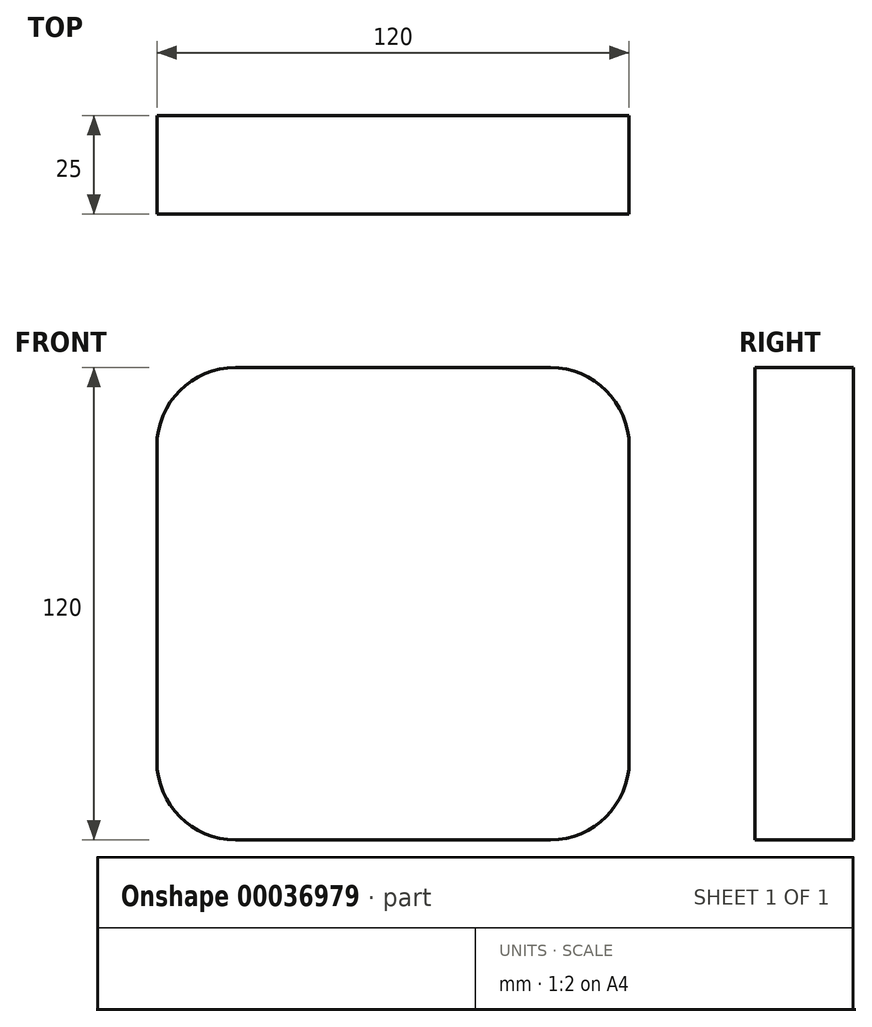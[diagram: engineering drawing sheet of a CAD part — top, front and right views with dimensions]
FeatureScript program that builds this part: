
annotation { "Feature Type Name" : "Feature", "Feature Type Description" : "" }
export const myFeature = defineFeature(function(context is Context, id is Id, definition is map)
    precondition{}
    {
        {
            var Q0;
            Q0=qCreatedBy(makeId("Front.planeOp"),FACE);
            var sketch = newSketch(context, id + "F0", { "sketchPlane" : qUnion([Q0])});
            skLineSegment(sketch, "E0.bottom", {"start": v(0, 0) * mm, "end": v(120, 0) * mm});
            skLineSegment(sketch, "E0.top", {"start": v(0, 120) * mm, "end": v(120, 120) * mm});
            skLineSegment(sketch, "E0.left", {"start": v(0, 0) * mm, "end": v(0, 120) * mm});
            skLineSegment(sketch, "E0.right", {"start": v(120, 0) * mm, "end": v(120, 120) * mm});
            skSolve(sketch);
        }
        {
            var Q0;
            Q0=makeQuery(id+"F0.imprint","IMPRINT",FACE,{"disambiguationData":[TD([[makeQuery(id+"F0.imprint","IMPRINT",EDGE,{"derivedFrom":sQuery(id+"F0.wireOp",EDGE,"E0.bottom")}),1.0]])]});
            extrude(context, id + "F1", {"entities" : qUnion([Q0]), "depth" : 25 * mm});
        }
        {
            var Q0;
            Q0=makeQuery(id+"F1.opExtrude","SWEPT_EDGE",EDGE,{"disambiguationData":[OSD([sQuery(id+"F0.wireOp",EDGE,"E0.bottom"),sQuery(id+"F0.wireOp",EDGE,"E0.right")])]});
            var Q1;
            Q1=makeQuery(id+"F1.opExtrude","SWEPT_EDGE",EDGE,{"disambiguationData":[OSD([sQuery(id+"F0.wireOp",EDGE,"E0.bottom"),sQuery(id+"F0.wireOp",EDGE,"E0.left")])]});
            var Q2;
            Q2=makeQuery(id+"F1.opExtrude","SWEPT_EDGE",EDGE,{"disambiguationData":[OSD([sQuery(id+"F0.wireOp",EDGE,"E0.top"),sQuery(id+"F0.wireOp",EDGE,"E0.right")])]});
            var Q3;
            Q3=makeQuery(id+"F1.opExtrude","SWEPT_EDGE",EDGE,{"disambiguationData":[OSD([sQuery(id+"F0.wireOp",EDGE,"E0.top"),sQuery(id+"F0.wireOp",EDGE,"E0.left")])]});
            fillet(context, id + "F2", {"entities" : qUnion([Q0, Q1, Q2, Q3]), "radius" : 20 * mm, "tangentPropagation" : true, "allowEdgeOverflow" : false});
        }
    });
